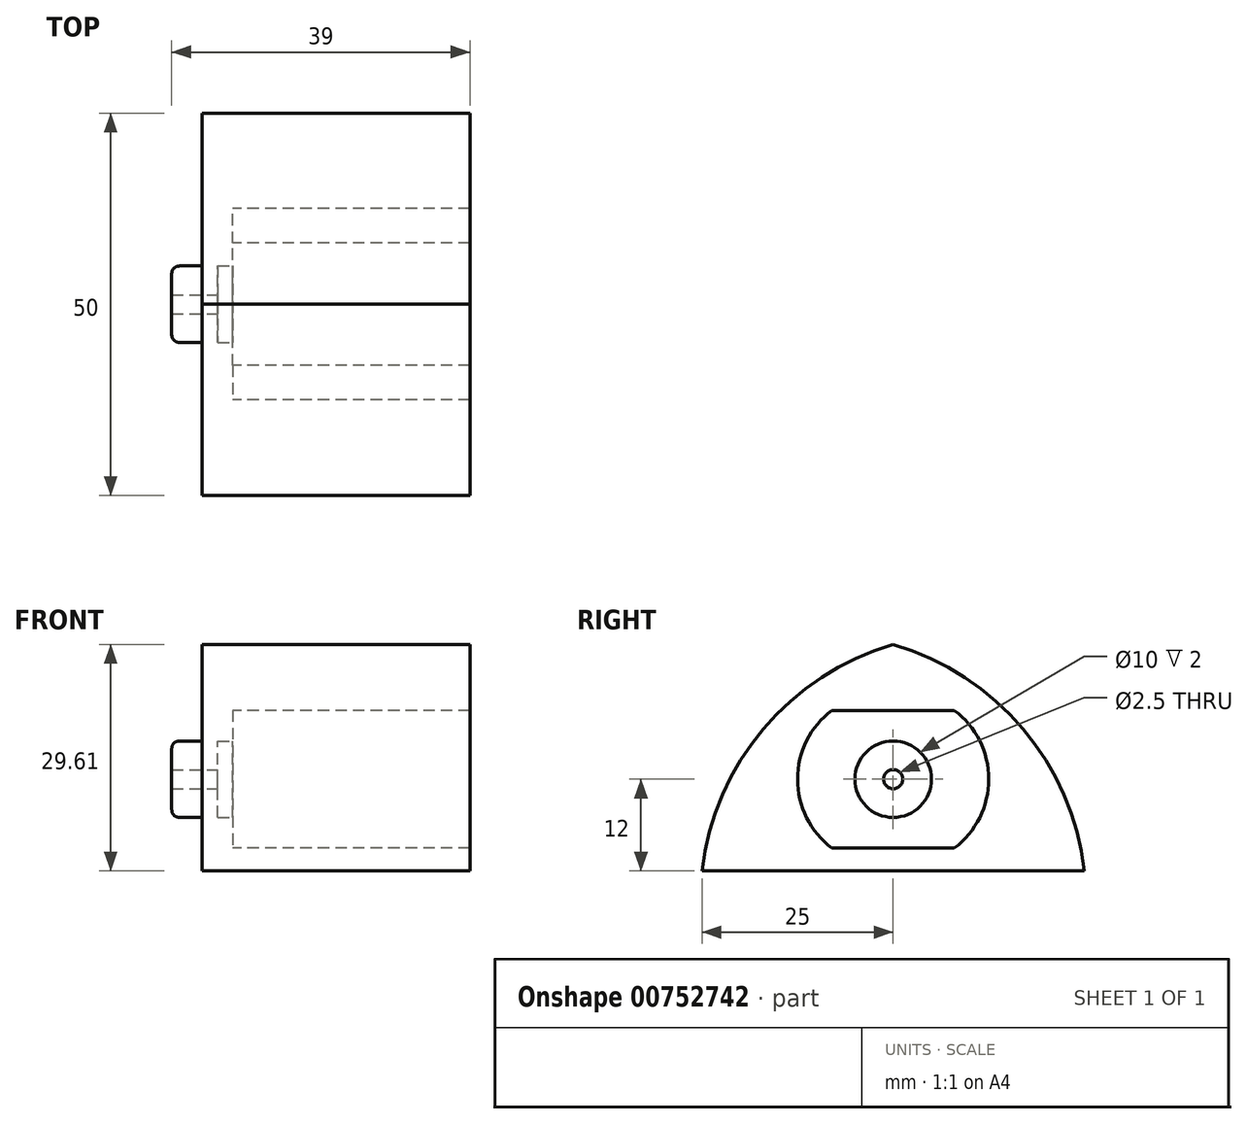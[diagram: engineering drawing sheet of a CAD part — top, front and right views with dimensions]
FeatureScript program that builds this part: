
annotation { "Feature Type Name" : "Feature", "Feature Type Description" : "" }
export const myFeature = defineFeature(function(context is Context, id is Id, definition is map)
    precondition{}
    {
        {
            var Q0;
            Q0=qCreatedBy(makeId("Right.planeOp"),FACE);
            var sketch = newSketch(context, id + "F0", { "sketchPlane" : qUnion([Q0])});
            skLineSegment(sketch, "E0.bottom", {"start": v(-79.83, 54.03) * mm, "end": v(-63.83, 54.03) * mm});
            skLineSegment(sketch, "E0.top", {"start": v(-79.83, 36.03) * mm, "end": v(-63.83, 36.03) * mm});
            skArc(sketch, "E1", {"start": v(-79.83, 54.03) * mm, "mid": v(-84.33, 45.03) * mm, "end": v(-79.83, 36.03) * mm});
            skArc(sketch, "E2", {"start": v(-63.83, 36.03) * mm, "mid": v(-59.33, 45.03) * mm, "end": v(-63.83, 54.03) * mm});
            skLineSegment(sketch, "E3.bottom", {"start": v(-96.83, 64.03) * mm, "end": v(-46.83, 64.03) * mm});
            skLineSegment(sketch, "E3.top", {"start": v(-96.83, 33.03) * mm, "end": v(-46.83, 33.03) * mm});
            skLineSegment(sketch, "E3.left", {"start": v(-96.83, 64.03) * mm, "end": v(-96.83, 33.03) * mm});
            skLineSegment(sketch, "E3.right", {"start": v(-46.83, 64.03) * mm, "end": v(-46.83, 33.03) * mm});
            skSolve(sketch);
        }
        {
            var Q0;
            Q0=makeQuery(id+"F0.imprint","IMPRINT",FACE,{"disambiguationData":[TD([[makeQuery(id+"F0.imprint","IMPRINT",EDGE,{"derivedFrom":sQuery(id+"F0.wireOp",EDGE,"E0.bottom")}),1.0]])]});
            extrude(context, id + "F1", {"entities" : qUnion([Q0]), "depth" : 35 * mm, "offsetDistance" : 25 * mm});
        }
        {
            var Q0;
            Q0=makeQuery(id+"F1.opExtrude","CAP_FACE",FACE,{"disambiguationData":[OSD([sQuery(id+"F0.wireOp",EDGE,"E0.bottom"),sQuery(id+"F0.wireOp",EDGE,"E0.top"),sQuery(id+"F0.wireOp",EDGE,"E1"),sQuery(id+"F0.wireOp",EDGE,"E2"),sQuery(id+"F0.wireOp",EDGE,"E3.bottom"),sQuery(id+"F0.wireOp",EDGE,"E3.top"),sQuery(id+"F0.wireOp",EDGE,"E3.left"),sQuery(id+"F0.wireOp",EDGE,"E3.right")])],"isStart":true});
            var sketch = newSketch(context, id + "F2", { "sketchPlane" : qUnion([Q0])});
            skLineSegment(sketch, "E4", {"start": v(63.83, 54.03) * mm, "end": v(79.83, 54.03) * mm});
            skLineSegment(sketch, "E5", {"start": v(63.83, 36.03) * mm, "end": v(79.83, 36.03) * mm});
            skArc(sketch, "E6", {"start": v(63.83, 54.03) * mm, "mid": v(59.33, 45.03) * mm, "end": v(63.83, 36.03) * mm});
            skArc(sketch, "E7", {"start": v(79.83, 36.03) * mm, "mid": v(84.33, 45.03) * mm, "end": v(79.83, 54.03) * mm});
            skSolve(sketch);
        }
        {
            var Q0;
            Q0=makeQuery(id+"F2.imprint","IMPRINT",FACE,{"disambiguationData":[TD([[makeQuery(id+"F2.imprint","IMPRINT",EDGE,{"derivedFrom":sQuery(id+"F2.wireOp",EDGE,"E4")}),1.0]])]});
            extrude(context, id + "F3", {"entities" : qUnion([Q0]), "operationType" : NewBodyOperationType.ADD, "oppositeDirection" : true, "depth" : 4 * mm, "offsetDistance" : 25 * mm});
        }
        {
            var Q0;
            Q0=makeQuery(id+"F3.opExtrude","CAP_FACE",FACE,{"disambiguationData":[OSD([sQuery(id+"F2.wireOp",EDGE,"E4"),sQuery(id+"F2.wireOp",EDGE,"E5"),sQuery(id+"F2.wireOp",EDGE,"E6"),sQuery(id+"F2.wireOp",EDGE,"E7")])],"isStart":false});
            var sketch = newSketch(context, id + "F4", { "sketchPlane" : qUnion([Q0])});
            skCircle(sketch, "E8", {"center": v(-71.83, 45.03) * mm, "radius": 5 * mm});
            skSolve(sketch);
        }
        {
            var Q0;
            Q0=makeQuery(id+"F4.imprint","IMPRINT",FACE,{"disambiguationData":[TD([[makeQuery(id+"F4.imprint","IMPRINT",EDGE,{"derivedFrom":sQuery(id+"F4.wireOp",EDGE,"E8")}),1.0]])]});
            extrude(context, id + "F5", {"entities" : qUnion([Q0]), "operationType" : NewBodyOperationType.REMOVE, "oppositeDirection" : true, "depth" : 2 * mm, "offsetDistance" : 25 * mm});
        }
        {
            var Q0;
            Q0=makeQuery(id+"F5.boolean.opBoolean","COPY",FACE,{"derivedFrom":makeQuery(id+"F5.opExtrude","CAP_FACE",FACE,{"disambiguationData":[OSD([sQuery(id+"F4.wireOp",EDGE,"E8")])],"isStart":false})});
            var sketch = newSketch(context, id + "F6", { "sketchPlane" : qUnion([Q0])});
            skCircle(sketch, "E9", {"center": v(-71.83, 45.03) * mm, "radius": 1.25 * mm});
            skSolve(sketch);
        }
        {
            var Q0;
            Q0=makeQuery(id+"F6.imprint","IMPRINT",FACE,{"disambiguationData":[TD([[makeQuery(id+"F6.imprint","IMPRINT",EDGE,{"derivedFrom":sQuery(id+"F6.wireOp",EDGE,"E9")}),1.0]])]});
            extrude(context, id + "F7", {"entities" : qUnion([Q0]), "operationType" : NewBodyOperationType.REMOVE, "oppositeDirection" : true, "depth" : 25 * mm, "offsetDistance" : 25 * mm});
        }
        {
            var Q0;
            Q0=makeQuery(id+"F3.boolean.opBoolean","MERGE",FACE,{"derivedFrom":[makeQuery(id+"F1.opExtrude","CAP_FACE",FACE,{"disambiguationData":[OSD([sQuery(id+"F0.wireOp",EDGE,"E0.bottom"),sQuery(id+"F0.wireOp",EDGE,"E0.top"),sQuery(id+"F0.wireOp",EDGE,"E1"),sQuery(id+"F0.wireOp",EDGE,"E2"),sQuery(id+"F0.wireOp",EDGE,"E3.bottom"),sQuery(id+"F0.wireOp",EDGE,"E3.top"),sQuery(id+"F0.wireOp",EDGE,"E3.left"),sQuery(id+"F0.wireOp",EDGE,"E3.right")])],"isStart":true}),makeQuery(id+"F3.opExtrude","CAP_FACE",FACE,{"disambiguationData":[OSD([sQuery(id+"F2.wireOp",EDGE,"E4"),sQuery(id+"F2.wireOp",EDGE,"E5"),sQuery(id+"F2.wireOp",EDGE,"E6"),sQuery(id+"F2.wireOp",EDGE,"E7")])],"isStart":true})]});
            var sketch = newSketch(context, id + "F8", { "sketchPlane" : qUnion([Q0])});
            skCircle(sketch, "E10", {"center": v(71.83, 45.03) * mm, "radius": 1.25 * mm});
            skCircle(sketch, "E11", {"center": v(71.83, 45.03) * mm, "radius": 5 * mm});
            skSolve(sketch);
        }
        {
            var Q0;
            Q0=makeQuery(id+"F8.imprint","IMPRINT",FACE,{"disambiguationData":[TD([[makeQuery(id+"F8.imprint","IMPRINT",EDGE,{"derivedFrom":sQuery(id+"F8.wireOp",EDGE,"E10")}),1.0]])]});
            extrude(context, id + "F9", {"entities" : qUnion([Q0]), "operationType" : NewBodyOperationType.ADD, "depth" : 4 * mm, "offsetDistance" : 25 * mm});
        }
        {
            var Q0;
            Q0=makeQuery(id+"F9.opExtrude","CAP_EDGE",EDGE,{"disambiguationData":[OSD([sQuery(id+"F8.wireOp",EDGE,"E11")])],"isStart":false});
            var Q1;
            Q1=makeQuery(id+"F9.opExtrude","CAP_EDGE",EDGE,{"disambiguationData":[OSD([sQuery(id+"F8.wireOp",EDGE,"E11")])],"isStart":true});
            fillet(context, id + "F10", {"entities" : qUnion([Q0, Q1]), "radius" : 1 * mm, "tangentPropagation" : true, "allowEdgeOverflow" : false});
        }
        {
            var Q0;
            Q0=makeQuery(id+"F1.opExtrude","SWEPT_EDGE",EDGE,{"disambiguationData":[OSD([sQuery(id+"F0.wireOp",EDGE,"E3.bottom"),sQuery(id+"F0.wireOp",EDGE,"E3.left")])]});
            var Q1;
            Q1=makeQuery(id+"F1.opExtrude","SWEPT_EDGE",EDGE,{"disambiguationData":[OSD([sQuery(id+"F0.wireOp",EDGE,"E3.bottom"),sQuery(id+"F0.wireOp",EDGE,"E3.right")])]});
            fillet(context, id + "F11", {"entities" : qUnion([Q0, Q1]), "radius" : 35 * mm, "tangentPropagation" : true, "allowEdgeOverflow" : false});
        }
    });
